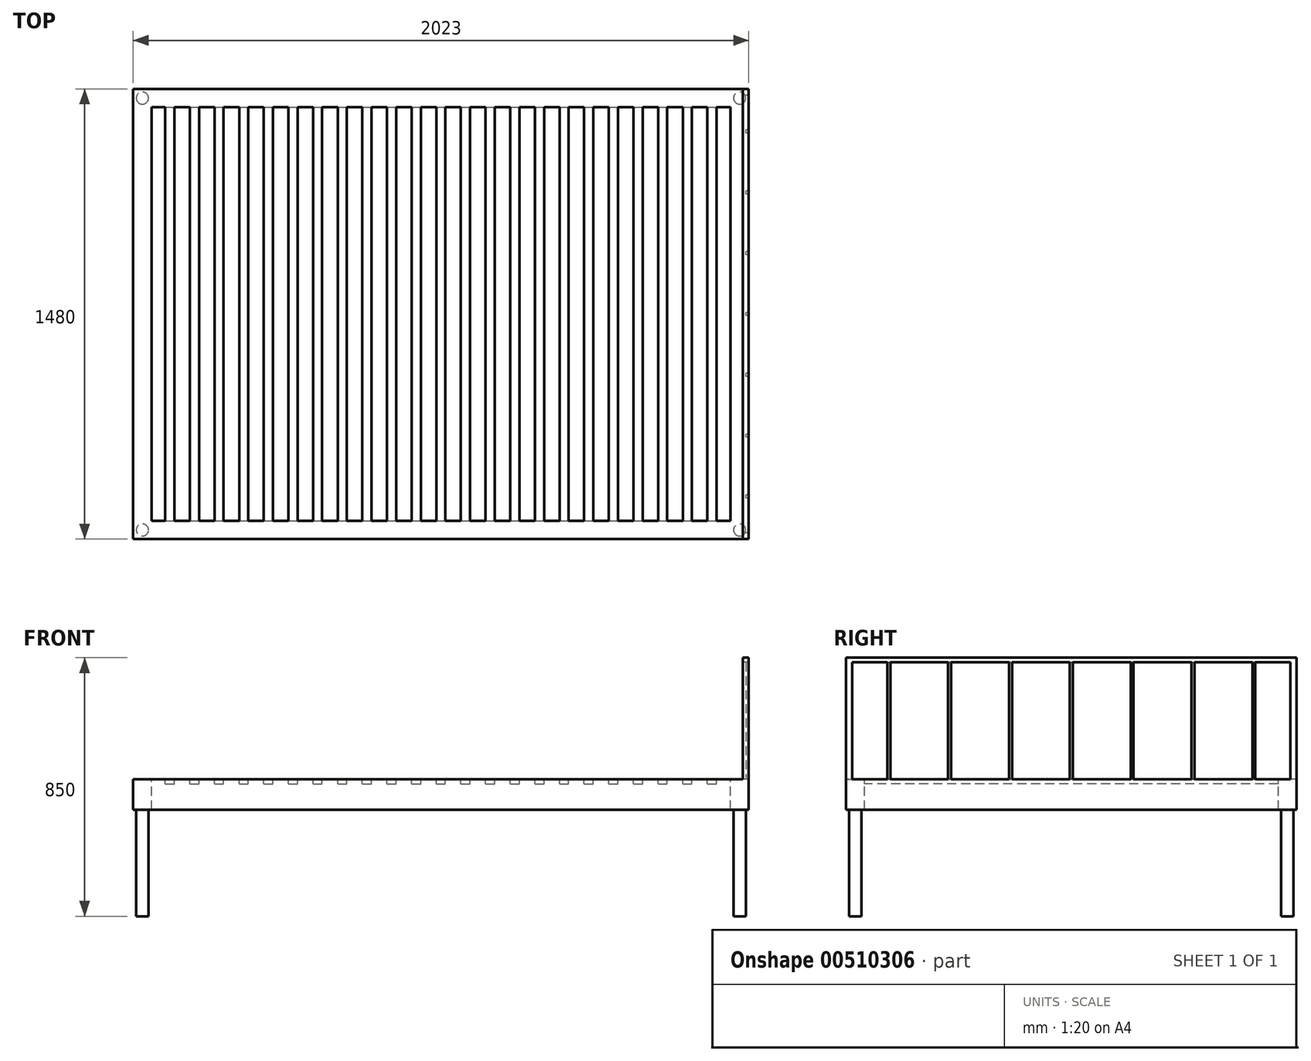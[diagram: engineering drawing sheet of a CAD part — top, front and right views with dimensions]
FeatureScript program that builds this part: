
annotation { "Feature Type Name" : "Feature", "Feature Type Description" : "" }
export const myFeature = defineFeature(function(context is Context, id is Id, definition is map)
    precondition{}
    {
        {
            var Q0;
            Q0=qCreatedBy(makeId("Top.planeOp"),FACE);
            var sketch = newSketch(context, id + "F0", { "sketchPlane" : qUnion([Q0])});
            skLineSegment(sketch, "E0.bottom", {"start": v(-1011.5, 740) * mm, "end": v(1011.5, 740) * mm});
            skLineSegment(sketch, "E0.top", {"start": v(-1011.5, -740) * mm, "end": v(1011.5, -740) * mm});
            skLineSegment(sketch, "E0.left", {"start": v(-1011.5, 740) * mm, "end": v(-1011.5, -740) * mm});
            skLineSegment(sketch, "E0.right", {"start": v(1011.5, 740) * mm, "end": v(1011.5, -740) * mm});
            skPoint(sketch, "E0.middle", {"position": v(0, 0) * mm});
            skLineSegment(sketch, "E1.bottom", {"start": v(-951.5, 680) * mm, "end": v(951.5, 680) * mm});
            skLineSegment(sketch, "E1.top", {"start": v(-951.5, -680) * mm, "end": v(951.5, -680) * mm});
            skLineSegment(sketch, "E1.left", {"start": v(-951.5, 680) * mm, "end": v(-951.5, -680) * mm});
            skLineSegment(sketch, "E1.right", {"start": v(951.5, 680) * mm, "end": v(951.5, -680) * mm});
            skLineSegment(sketch, "E2", {"start": v(-906.5, 680) * mm, "end": v(-906.5, -680) * mm});
            skLineSegment(sketch, "E3", {"start": v(-906.5, -680) * mm, "end": v(-876.5, -680) * mm});
            skLineSegment(sketch, "E4", {"start": v(-876.5, -680) * mm, "end": v(-876.5, 680) * mm});
            skLineSegment(sketch, "E5.1.0.0", {"start": v(-795.5, -680) * mm, "end": v(-795.5, 680) * mm});
            skLineSegment(sketch, "E5.1.0.1", {"start": v(-825.5, 680) * mm, "end": v(-825.5, -680) * mm});
            skLineSegment(sketch, "E5.2.0.0", {"start": v(-714.5, -680) * mm, "end": v(-714.5, 680) * mm});
            skLineSegment(sketch, "E5.2.0.1", {"start": v(-744.5, 680) * mm, "end": v(-744.5, -680) * mm});
            skLineSegment(sketch, "E5.3.0.0", {"start": v(-633.5, -680) * mm, "end": v(-633.5, 680) * mm});
            skLineSegment(sketch, "E5.3.0.1", {"start": v(-663.5, 680) * mm, "end": v(-663.5, -680) * mm});
            skLineSegment(sketch, "E5.4.0.0", {"start": v(-552.5, -680) * mm, "end": v(-552.5, 680) * mm});
            skLineSegment(sketch, "E5.4.0.1", {"start": v(-582.5, 680) * mm, "end": v(-582.5, -680) * mm});
            skLineSegment(sketch, "E5.5.0.0", {"start": v(-471.5, -680) * mm, "end": v(-471.5, 680) * mm});
            skLineSegment(sketch, "E5.5.0.1", {"start": v(-501.5, 680) * mm, "end": v(-501.5, -680) * mm});
            skLineSegment(sketch, "E5.6.0.0", {"start": v(-390.5, -680) * mm, "end": v(-390.5, 680) * mm});
            skLineSegment(sketch, "E5.6.0.1", {"start": v(-420.5, 680) * mm, "end": v(-420.5, -680) * mm});
            skLineSegment(sketch, "E5.7.0.0", {"start": v(-309.5, -680) * mm, "end": v(-309.5, 680) * mm});
            skLineSegment(sketch, "E5.7.0.1", {"start": v(-339.5, 680) * mm, "end": v(-339.5, -680) * mm});
            skLineSegment(sketch, "E5.8.0.0", {"start": v(-228.5, -680) * mm, "end": v(-228.5, 680) * mm});
            skLineSegment(sketch, "E5.8.0.1", {"start": v(-258.5, 680) * mm, "end": v(-258.5, -680) * mm});
            skLineSegment(sketch, "E5.9.0.0", {"start": v(-147.5, -680) * mm, "end": v(-147.5, 680) * mm});
            skLineSegment(sketch, "E5.9.0.1", {"start": v(-177.5, 680) * mm, "end": v(-177.5, -680) * mm});
            skLineSegment(sketch, "E5.10.0.0", {"start": v(-66.5, -680) * mm, "end": v(-66.5, 680) * mm});
            skLineSegment(sketch, "E5.10.0.1", {"start": v(-96.5, 680) * mm, "end": v(-96.5, -680) * mm});
            skLineSegment(sketch, "E5.11.0.0", {"start": v(14.5, -680) * mm, "end": v(14.5, 680) * mm});
            skLineSegment(sketch, "E5.11.0.1", {"start": v(-15.5, 680) * mm, "end": v(-15.5, -680) * mm});
            skLineSegment(sketch, "E5.12.0.0", {"start": v(95.5, -680) * mm, "end": v(95.5, 680) * mm});
            skLineSegment(sketch, "E5.12.0.1", {"start": v(65.5, 680) * mm, "end": v(65.5, -680) * mm});
            skLineSegment(sketch, "E5.13.0.0", {"start": v(176.5, -680) * mm, "end": v(176.5, 680) * mm});
            skLineSegment(sketch, "E5.13.0.1", {"start": v(146.5, 680) * mm, "end": v(146.5, -680) * mm});
            skLineSegment(sketch, "E5.14.0.0", {"start": v(257.5, -680) * mm, "end": v(257.5, 680) * mm});
            skLineSegment(sketch, "E5.14.0.1", {"start": v(227.5, 680) * mm, "end": v(227.5, -680) * mm});
            skLineSegment(sketch, "E5.15.0.0", {"start": v(338.5, -680) * mm, "end": v(338.5, 680) * mm});
            skLineSegment(sketch, "E5.15.0.1", {"start": v(308.5, 680) * mm, "end": v(308.5, -680) * mm});
            skLineSegment(sketch, "E5.16.0.0", {"start": v(419.5, -680) * mm, "end": v(419.5, 680) * mm});
            skLineSegment(sketch, "E5.16.0.1", {"start": v(389.5, 680) * mm, "end": v(389.5, -680) * mm});
            skLineSegment(sketch, "E5.17.0.0", {"start": v(500.5, -680) * mm, "end": v(500.5, 680) * mm});
            skLineSegment(sketch, "E5.17.0.1", {"start": v(470.5, 680) * mm, "end": v(470.5, -680) * mm});
            skLineSegment(sketch, "E5.18.0.0", {"start": v(581.5, -680) * mm, "end": v(581.5, 680) * mm});
            skLineSegment(sketch, "E5.18.0.1", {"start": v(551.5, 680) * mm, "end": v(551.5, -680) * mm});
            skLineSegment(sketch, "E5.19.0.0", {"start": v(662.5, -680) * mm, "end": v(662.5, 680) * mm});
            skLineSegment(sketch, "E5.19.0.1", {"start": v(632.5, 680) * mm, "end": v(632.5, -680) * mm});
            skLineSegment(sketch, "E5.20.0.0", {"start": v(743.5, -680) * mm, "end": v(743.5, 680) * mm});
            skLineSegment(sketch, "E5.20.0.1", {"start": v(713.5, 680) * mm, "end": v(713.5, -680) * mm});
            skLineSegment(sketch, "E5.21.0.0", {"start": v(824.5, -680) * mm, "end": v(824.5, 680) * mm});
            skLineSegment(sketch, "E5.21.0.1", {"start": v(794.5, 680) * mm, "end": v(794.5, -680) * mm});
            skLineSegment(sketch, "E5.22.0.0", {"start": v(905.5, -680) * mm, "end": v(905.5, 680) * mm});
            skLineSegment(sketch, "E5.22.0.1", {"start": v(875.5, 680) * mm, "end": v(875.5, -680) * mm});
            skLineSegment(sketch, "E5.direction1", {"start": v(-876.5, -680) * mm, "end": v(-795.5, -680) * mm, "construction": true});
            skSolve(sketch);
        }
        {
            var Q0;
            Q0=makeQuery(id+"F0.imprint","IMPRINT",FACE,{"disambiguationData":[TD([[makeQuery(id+"F0.imprint","IMPRINT",EDGE,{"derivedFrom":sQuery(id+"F0.wireOp",EDGE,"E0.bottom")}),-1.0]])]});
            var Q1;
            {var subQ0=sQuery(id+"F0.wireOp",EDGE,"E2");Q1=makeQuery(id+"F0.imprint","IMPRINT",FACE,{"disambiguationData":[TD([[makeQuery(id+"F0.imprint","IMPRINT",EDGE,{"derivedFrom":subQ0}),1.0]])]});}
            var Q2;
            {var subQ0=sQuery(id+"F0.wireOp",EDGE,"E5.1.0.0");Q2=makeQuery(id+"F0.imprint","IMPRINT",FACE,{"disambiguationData":[TD([[makeQuery(id+"F0.imprint","IMPRINT",EDGE,{"derivedFrom":subQ0}),1.0]])]});}
            var Q3;
            {var subQ0=sQuery(id+"F0.wireOp",EDGE,"E5.2.0.0");Q3=makeQuery(id+"F0.imprint","IMPRINT",FACE,{"disambiguationData":[TD([[makeQuery(id+"F0.imprint","IMPRINT",EDGE,{"derivedFrom":subQ0}),1.0]])]});}
            var Q4;
            {var subQ0=sQuery(id+"F0.wireOp",EDGE,"E5.3.0.0");Q4=makeQuery(id+"F0.imprint","IMPRINT",FACE,{"disambiguationData":[TD([[makeQuery(id+"F0.imprint","IMPRINT",EDGE,{"derivedFrom":subQ0}),1.0]])]});}
            var Q5;
            {var subQ0=sQuery(id+"F0.wireOp",EDGE,"E5.4.0.0");Q5=makeQuery(id+"F0.imprint","IMPRINT",FACE,{"disambiguationData":[TD([[makeQuery(id+"F0.imprint","IMPRINT",EDGE,{"derivedFrom":subQ0}),1.0]])]});}
            var Q6;
            {var subQ0=sQuery(id+"F0.wireOp",EDGE,"E5.5.0.0");Q6=makeQuery(id+"F0.imprint","IMPRINT",FACE,{"disambiguationData":[TD([[makeQuery(id+"F0.imprint","IMPRINT",EDGE,{"derivedFrom":subQ0}),1.0]])]});}
            var Q7;
            {var subQ0=sQuery(id+"F0.wireOp",EDGE,"E5.6.0.0");Q7=makeQuery(id+"F0.imprint","IMPRINT",FACE,{"disambiguationData":[TD([[makeQuery(id+"F0.imprint","IMPRINT",EDGE,{"derivedFrom":subQ0}),1.0]])]});}
            var Q8;
            {var subQ0=sQuery(id+"F0.wireOp",EDGE,"E5.7.0.0");Q8=makeQuery(id+"F0.imprint","IMPRINT",FACE,{"disambiguationData":[TD([[makeQuery(id+"F0.imprint","IMPRINT",EDGE,{"derivedFrom":subQ0}),1.0]])]});}
            var Q9;
            {var subQ0=sQuery(id+"F0.wireOp",EDGE,"E5.8.0.0");Q9=makeQuery(id+"F0.imprint","IMPRINT",FACE,{"disambiguationData":[TD([[makeQuery(id+"F0.imprint","IMPRINT",EDGE,{"derivedFrom":subQ0}),1.0]])]});}
            var Q10;
            {var subQ0=sQuery(id+"F0.wireOp",EDGE,"E5.9.0.0");Q10=makeQuery(id+"F0.imprint","IMPRINT",FACE,{"disambiguationData":[TD([[makeQuery(id+"F0.imprint","IMPRINT",EDGE,{"derivedFrom":subQ0}),1.0]])]});}
            var Q11;
            {var subQ0=sQuery(id+"F0.wireOp",EDGE,"E5.10.0.0");Q11=makeQuery(id+"F0.imprint","IMPRINT",FACE,{"disambiguationData":[TD([[makeQuery(id+"F0.imprint","IMPRINT",EDGE,{"derivedFrom":subQ0}),1.0]])]});}
            var Q12;
            {var subQ0=sQuery(id+"F0.wireOp",EDGE,"E5.11.0.0");Q12=makeQuery(id+"F0.imprint","IMPRINT",FACE,{"disambiguationData":[TD([[makeQuery(id+"F0.imprint","IMPRINT",EDGE,{"derivedFrom":subQ0}),1.0]])]});}
            var Q13;
            {var subQ0=sQuery(id+"F0.wireOp",EDGE,"E5.12.0.0");Q13=makeQuery(id+"F0.imprint","IMPRINT",FACE,{"disambiguationData":[TD([[makeQuery(id+"F0.imprint","IMPRINT",EDGE,{"derivedFrom":subQ0}),1.0]])]});}
            var Q14;
            {var subQ0=sQuery(id+"F0.wireOp",EDGE,"E5.13.0.0");Q14=makeQuery(id+"F0.imprint","IMPRINT",FACE,{"disambiguationData":[TD([[makeQuery(id+"F0.imprint","IMPRINT",EDGE,{"derivedFrom":subQ0}),1.0]])]});}
            var Q15;
            {var subQ0=sQuery(id+"F0.wireOp",EDGE,"E5.14.0.0");Q15=makeQuery(id+"F0.imprint","IMPRINT",FACE,{"disambiguationData":[TD([[makeQuery(id+"F0.imprint","IMPRINT",EDGE,{"derivedFrom":subQ0}),1.0]])]});}
            var Q16;
            {var subQ0=sQuery(id+"F0.wireOp",EDGE,"E5.15.0.0");Q16=makeQuery(id+"F0.imprint","IMPRINT",FACE,{"disambiguationData":[TD([[makeQuery(id+"F0.imprint","IMPRINT",EDGE,{"derivedFrom":subQ0}),1.0]])]});}
            var Q17;
            {var subQ0=sQuery(id+"F0.wireOp",EDGE,"E5.16.0.0");Q17=makeQuery(id+"F0.imprint","IMPRINT",FACE,{"disambiguationData":[TD([[makeQuery(id+"F0.imprint","IMPRINT",EDGE,{"derivedFrom":subQ0}),1.0]])]});}
            var Q18;
            {var subQ0=sQuery(id+"F0.wireOp",EDGE,"E5.17.0.0");Q18=makeQuery(id+"F0.imprint","IMPRINT",FACE,{"disambiguationData":[TD([[makeQuery(id+"F0.imprint","IMPRINT",EDGE,{"derivedFrom":subQ0}),1.0]])]});}
            var Q19;
            {var subQ0=sQuery(id+"F0.wireOp",EDGE,"E5.18.0.0");Q19=makeQuery(id+"F0.imprint","IMPRINT",FACE,{"disambiguationData":[TD([[makeQuery(id+"F0.imprint","IMPRINT",EDGE,{"derivedFrom":subQ0}),1.0]])]});}
            var Q20;
            {var subQ0=sQuery(id+"F0.wireOp",EDGE,"E5.19.0.0");Q20=makeQuery(id+"F0.imprint","IMPRINT",FACE,{"disambiguationData":[TD([[makeQuery(id+"F0.imprint","IMPRINT",EDGE,{"derivedFrom":subQ0}),1.0]])]});}
            var Q21;
            {var subQ0=sQuery(id+"F0.wireOp",EDGE,"E5.20.0.0");Q21=makeQuery(id+"F0.imprint","IMPRINT",FACE,{"disambiguationData":[TD([[makeQuery(id+"F0.imprint","IMPRINT",EDGE,{"derivedFrom":subQ0}),1.0]])]});}
            var Q22;
            {var subQ0=sQuery(id+"F0.wireOp",EDGE,"E5.21.0.0");Q22=makeQuery(id+"F0.imprint","IMPRINT",FACE,{"disambiguationData":[TD([[makeQuery(id+"F0.imprint","IMPRINT",EDGE,{"derivedFrom":subQ0}),1.0]])]});}
            var Q23;
            {var subQ0=sQuery(id+"F0.wireOp",EDGE,"E5.22.0.0");Q23=makeQuery(id+"F0.imprint","IMPRINT",FACE,{"disambiguationData":[TD([[makeQuery(id+"F0.imprint","IMPRINT",EDGE,{"derivedFrom":subQ0}),1.0]])]});}
            extrude(context, id + "F1", {"entities" : qUnion([Q0, Q1, Q2, Q3, Q4, Q5, Q6, Q7, Q8, Q9, Q10, Q11, Q12, Q13, Q14, Q15, Q16, Q17, Q18, Q19, Q20, Q21, Q22, Q23]), "oppositeDirection" : true, "depth" : 15 * mm});
        }
        {
            var Q0;
            Q0=qSketchRegion(id+"F0",true);
            extrude(context, id + "F2", {"entities" : qUnion([Q0]), "operationType" : NewBodyOperationType.ADD, "oppositeDirection" : true, "depth" : 100 * mm});
        }
        {
            var Q0;
            Q0=makeQuery(id+"F2.opExtrude","CAP_FACE",FACE,{"disambiguationData":[OSD([sQuery(id+"F0.wireOp",EDGE,"E0.bottom"),sQuery(id+"F0.wireOp",EDGE,"E0.top"),sQuery(id+"F0.wireOp",EDGE,"E0.left"),sQuery(id+"F0.wireOp",EDGE,"E0.right"),sQuery(id+"F0.wireOp",EDGE,"E1.bottom"),sQuery(id+"F0.wireOp",EDGE,"E1.top"),sQuery(id+"F0.wireOp",EDGE,"E1.left"),sQuery(id+"F0.wireOp",EDGE,"E1.right"),sQuery(id+"F0.wireOp",EDGE,"E3")])],"isStart":false});
            var sketch = newSketch(context, id + "F3", { "sketchPlane" : qUnion([Q0])});
            skCircle(sketch, "E6", {"center": v(-981.5, 710) * mm, "radius": 20 * mm});
            skCircle(sketch, "E7", {"center": v(981.5, 710) * mm, "radius": 20 * mm});
            skCircle(sketch, "E8", {"center": v(981.5, -710) * mm, "radius": 20 * mm});
            skCircle(sketch, "E9", {"center": v(-981.5, -710) * mm, "radius": 20 * mm});
            skSolve(sketch);
        }
        {
            var Q0;
            Q0=qSketchRegion(id+"F3",true);
            extrude(context, id + "F4", {"entities" : qUnion([Q0]), "operationType" : NewBodyOperationType.ADD, "depth" : 350 * mm});
        }
        {
            var Q0;
            Q0=makeQuery(id+"F1.opExtrude","CAP_FACE",FACE,{"disambiguationData":[OSD([sQuery(id+"F0.wireOp",EDGE,"E0.bottom"),sQuery(id+"F0.wireOp",EDGE,"E0.top"),sQuery(id+"F0.wireOp",EDGE,"E0.left"),sQuery(id+"F0.wireOp",EDGE,"E0.right"),sQuery(id+"F0.wireOp",EDGE,"E1.bottom"),sQuery(id+"F0.wireOp",EDGE,"E1.top"),sQuery(id+"F0.wireOp",EDGE,"E1.left"),sQuery(id+"F0.wireOp",EDGE,"E1.right"),sQuery(id+"F0.wireOp",EDGE,"E2"),sQuery(id+"F0.wireOp",EDGE,"E4"),sQuery(id+"F0.wireOp",EDGE,"E5.1.0.0"),sQuery(id+"F0.wireOp",EDGE,"E5.1.0.1"),sQuery(id+"F0.wireOp",EDGE,"E5.2.0.0"),sQuery(id+"F0.wireOp",EDGE,"E5.2.0.1"),sQuery(id+"F0.wireOp",EDGE,"E5.3.0.0"),sQuery(id+"F0.wireOp",EDGE,"E5.3.0.1"),sQuery(id+"F0.wireOp",EDGE,"E5.4.0.0"),sQuery(id+"F0.wireOp",EDGE,"E5.4.0.1"),sQuery(id+"F0.wireOp",EDGE,"E5.5.0.0"),sQuery(id+"F0.wireOp",EDGE,"E5.5.0.1"),sQuery(id+"F0.wireOp",EDGE,"E5.6.0.0"),sQuery(id+"F0.wireOp",EDGE,"E5.6.0.1"),sQuery(id+"F0.wireOp",EDGE,"E5.7.0.0"),sQuery(id+"F0.wireOp",EDGE,"E5.7.0.1"),sQuery(id+"F0.wireOp",EDGE,"E5.8.0.0"),sQuery(id+"F0.wireOp",EDGE,"E5.8.0.1"),sQuery(id+"F0.wireOp",EDGE,"E5.9.0.0"),sQuery(id+"F0.wireOp",EDGE,"E5.9.0.1"),sQuery(id+"F0.wireOp",EDGE,"E5.10.0.0"),sQuery(id+"F0.wireOp",EDGE,"E5.10.0.1"),sQuery(id+"F0.wireOp",EDGE,"E5.11.0.0"),sQuery(id+"F0.wireOp",EDGE,"E5.11.0.1"),sQuery(id+"F0.wireOp",EDGE,"E5.12.0.0"),sQuery(id+"F0.wireOp",EDGE,"E5.12.0.1"),sQuery(id+"F0.wireOp",EDGE,"E5.13.0.0"),sQuery(id+"F0.wireOp",EDGE,"E5.13.0.1"),sQuery(id+"F0.wireOp",EDGE,"E5.14.0.0"),sQuery(id+"F0.wireOp",EDGE,"E5.14.0.1"),sQuery(id+"F0.wireOp",EDGE,"E5.15.0.0"),sQuery(id+"F0.wireOp",EDGE,"E5.15.0.1"),sQuery(id+"F0.wireOp",EDGE,"E5.16.0.0"),sQuery(id+"F0.wireOp",EDGE,"E5.16.0.1"),sQuery(id+"F0.wireOp",EDGE,"E5.17.0.0"),sQuery(id+"F0.wireOp",EDGE,"E5.17.0.1"),sQuery(id+"F0.wireOp",EDGE,"E5.18.0.0"),sQuery(id+"F0.wireOp",EDGE,"E5.18.0.1"),sQuery(id+"F0.wireOp",EDGE,"E5.19.0.0"),sQuery(id+"F0.wireOp",EDGE,"E5.19.0.1"),sQuery(id+"F0.wireOp",EDGE,"E5.20.0.0"),sQuery(id+"F0.wireOp",EDGE,"E5.20.0.1"),sQuery(id+"F0.wireOp",EDGE,"E5.21.0.0"),sQuery(id+"F0.wireOp",EDGE,"E5.21.0.1"),sQuery(id+"F0.wireOp",EDGE,"E5.22.0.0"),sQuery(id+"F0.wireOp",EDGE,"E5.22.0.1")])],"isStart":true});
            var sketch = newSketch(context, id + "F5", { "sketchPlane" : qUnion([Q0])});
            skLineSegment(sketch, "E10.bottom", {"start": v(1011.5, 740) * mm, "end": v(991.5, 740) * mm});
            skLineSegment(sketch, "E10.top", {"start": v(1011.5, 720) * mm, "end": v(991.5, 720) * mm});
            skLineSegment(sketch, "E10.left", {"start": v(1011.5, 740) * mm, "end": v(1011.5, 720) * mm});
            skLineSegment(sketch, "E10.right", {"start": v(991.5, 740) * mm, "end": v(991.5, 720) * mm});
            skLineSegment(sketch, "E11.bottom", {"start": v(1011.5, -740) * mm, "end": v(991.5, -740) * mm});
            skLineSegment(sketch, "E11.top", {"start": v(1011.5, -720) * mm, "end": v(991.5, -720) * mm});
            skLineSegment(sketch, "E11.left", {"start": v(1011.5, -740) * mm, "end": v(1011.5, -720) * mm});
            skLineSegment(sketch, "E11.right", {"start": v(991.5, -740) * mm, "end": v(991.5, -720) * mm});
            skLineSegment(sketch, "E12.bottom", {"start": v(1011.5, -605) * mm, "end": v(1001.5, -605) * mm});
            skLineSegment(sketch, "E12.top", {"start": v(1011.5, -595) * mm, "end": v(1001.5, -595) * mm});
            skLineSegment(sketch, "E12.left", {"start": v(1011.5, -605) * mm, "end": v(1011.5, -595) * mm});
            skLineSegment(sketch, "E12.right", {"start": v(1001.5, -605) * mm, "end": v(1001.5, -595) * mm});
            skLineSegment(sketch, "E13.0.1.0", {"start": v(1011.5, -395) * mm, "end": v(1001.5, -395) * mm});
            skLineSegment(sketch, "E13.0.1.1", {"start": v(1001.5, -405) * mm, "end": v(1001.5, -395) * mm});
            skLineSegment(sketch, "E13.0.1.2", {"start": v(1011.5, -405) * mm, "end": v(1001.5, -405) * mm});
            skLineSegment(sketch, "E13.0.1.3", {"start": v(1011.5, -405) * mm, "end": v(1011.5, -395) * mm});
            skLineSegment(sketch, "E13.0.2.0", {"start": v(1011.5, -195) * mm, "end": v(1001.5, -195) * mm});
            skLineSegment(sketch, "E13.0.2.1", {"start": v(1001.5, -205) * mm, "end": v(1001.5, -195) * mm});
            skLineSegment(sketch, "E13.0.2.2", {"start": v(1011.5, -205) * mm, "end": v(1001.5, -205) * mm});
            skLineSegment(sketch, "E13.0.2.3", {"start": v(1011.5, -205) * mm, "end": v(1011.5, -195) * mm});
            skLineSegment(sketch, "E13.0.3.0", {"start": v(1011.5, 5) * mm, "end": v(1001.5, 5) * mm});
            skLineSegment(sketch, "E13.0.3.1", {"start": v(1001.5, -5) * mm, "end": v(1001.5, 5) * mm});
            skLineSegment(sketch, "E13.0.3.2", {"start": v(1011.5, -5) * mm, "end": v(1001.5, -5) * mm});
            skLineSegment(sketch, "E13.0.3.3", {"start": v(1011.5, -5) * mm, "end": v(1011.5, 5) * mm});
            skLineSegment(sketch, "E13.0.4.0", {"start": v(1011.5, 205) * mm, "end": v(1001.5, 205) * mm});
            skLineSegment(sketch, "E13.0.4.1", {"start": v(1001.5, 195) * mm, "end": v(1001.5, 205) * mm});
            skLineSegment(sketch, "E13.0.4.2", {"start": v(1011.5, 195) * mm, "end": v(1001.5, 195) * mm});
            skLineSegment(sketch, "E13.0.4.3", {"start": v(1011.5, 195) * mm, "end": v(1011.5, 205) * mm});
            skLineSegment(sketch, "E13.direction1", {"start": v(1001.5, -595) * mm, "end": v(1026.5, -595) * mm, "construction": true});
            skLineSegment(sketch, "E13.direction2", {"start": v(1001.5, -595) * mm, "end": v(1001.5, -395) * mm, "construction": true});
            skLineSegment(sketch, "E14.0.0.5", {"start": v(1011.5, 405) * mm, "end": v(1001.5, 405) * mm});
            skLineSegment(sketch, "E14.3.0.5", {"start": v(1001.5, 395) * mm, "end": v(1001.5, 405) * mm});
            skLineSegment(sketch, "E14.6.0.5", {"start": v(1011.5, 395) * mm, "end": v(1001.5, 395) * mm});
            skLineSegment(sketch, "E14.9.0.5", {"start": v(1011.5, 395) * mm, "end": v(1011.5, 405) * mm});
            skLineSegment(sketch, "E14.0.0.6", {"start": v(1011.5, 605) * mm, "end": v(1001.5, 605) * mm});
            skLineSegment(sketch, "E14.3.0.6", {"start": v(1001.5, 595) * mm, "end": v(1001.5, 605) * mm});
            skLineSegment(sketch, "E14.6.0.6", {"start": v(1011.5, 595) * mm, "end": v(1001.5, 595) * mm});
            skLineSegment(sketch, "E14.9.0.6", {"start": v(1011.5, 595) * mm, "end": v(1011.5, 605) * mm});
            skSolve(sketch);
        }
        {
            var Q0;
            Q0=qSketchRegion(id+"F5",true);
            extrude(context, id + "F6", {"entities" : qUnion([Q0]), "operationType" : NewBodyOperationType.ADD, "depth" : 400 * mm});
        }
        {
            var Q0;
            {var subQ0=sQuery(id+"F0.wireOp",EDGE,"E0.top");Q0=makeQuery(id+"F6.boolean.opBoolean","MERGE",FACE,{"derivedFrom":[makeQuery(id+"F2.boolean.opBoolean","MERGE",FACE,{"derivedFrom":[makeQuery(id+"F1.opExtrude","SWEPT_FACE",FACE,{"disambiguationData":[OSD([subQ0])]}),makeQuery(id+"F2.opExtrude","SWEPT_FACE",FACE,{"disambiguationData":[OSD([subQ0])]})]}),makeQuery(id+"F6.opExtrude","SWEPT_FACE",FACE,{"disambiguationData":[OSD([sQuery(id+"F5.wireOp",EDGE,"E11.bottom")])]})]});}
            var sketch = newSketch(context, id + "F7", { "sketchPlane" : qUnion([Q0])});
            skLineSegment(sketch, "E15.bottom", {"start": v(1011.5, 400) * mm, "end": v(991.5, 400) * mm});
            skLineSegment(sketch, "E15.top", {"start": v(1011.5, 385) * mm, "end": v(991.5, 385) * mm});
            skLineSegment(sketch, "E15.left", {"start": v(1011.5, 400) * mm, "end": v(1011.5, 385) * mm});
            skLineSegment(sketch, "E15.right", {"start": v(991.5, 400) * mm, "end": v(991.5, 385) * mm});
            skSolve(sketch);
        }
        {
            var Q0;
            Q0=makeQuery(id+"F7.imprint","IMPRINT",FACE,{"disambiguationData":[TD([[makeQuery(id+"F7.imprint","IMPRINT",EDGE,{"derivedFrom":sQuery(id+"F7.wireOp",EDGE,"E15.bottom")}),-1.0]])]});
            var Q1;
            {var subQ0=sQuery(id+"F0.wireOp",EDGE,"E0.bottom");Q1=makeQuery(id+"F6.boolean.opBoolean","MERGE",FACE,{"derivedFrom":[makeQuery(id+"F2.boolean.opBoolean","MERGE",FACE,{"derivedFrom":[makeQuery(id+"F1.opExtrude","SWEPT_FACE",FACE,{"disambiguationData":[OSD([subQ0])]}),makeQuery(id+"F2.opExtrude","SWEPT_FACE",FACE,{"disambiguationData":[OSD([subQ0])]})]}),makeQuery(id+"F6.opExtrude","SWEPT_FACE",FACE,{"disambiguationData":[OSD([sQuery(id+"F5.wireOp",EDGE,"E10.bottom")])]})]});}
            extrude(context, id + "F8", {"entities" : qUnion([Q0]), "operationType" : NewBodyOperationType.ADD, "endBound" : BoundingType.UP_TO_SURFACE, "oppositeDirection" : true, "endBoundEntityFace" : qUnion([Q1]), "depth" : 25 * mm});
        }
    });
